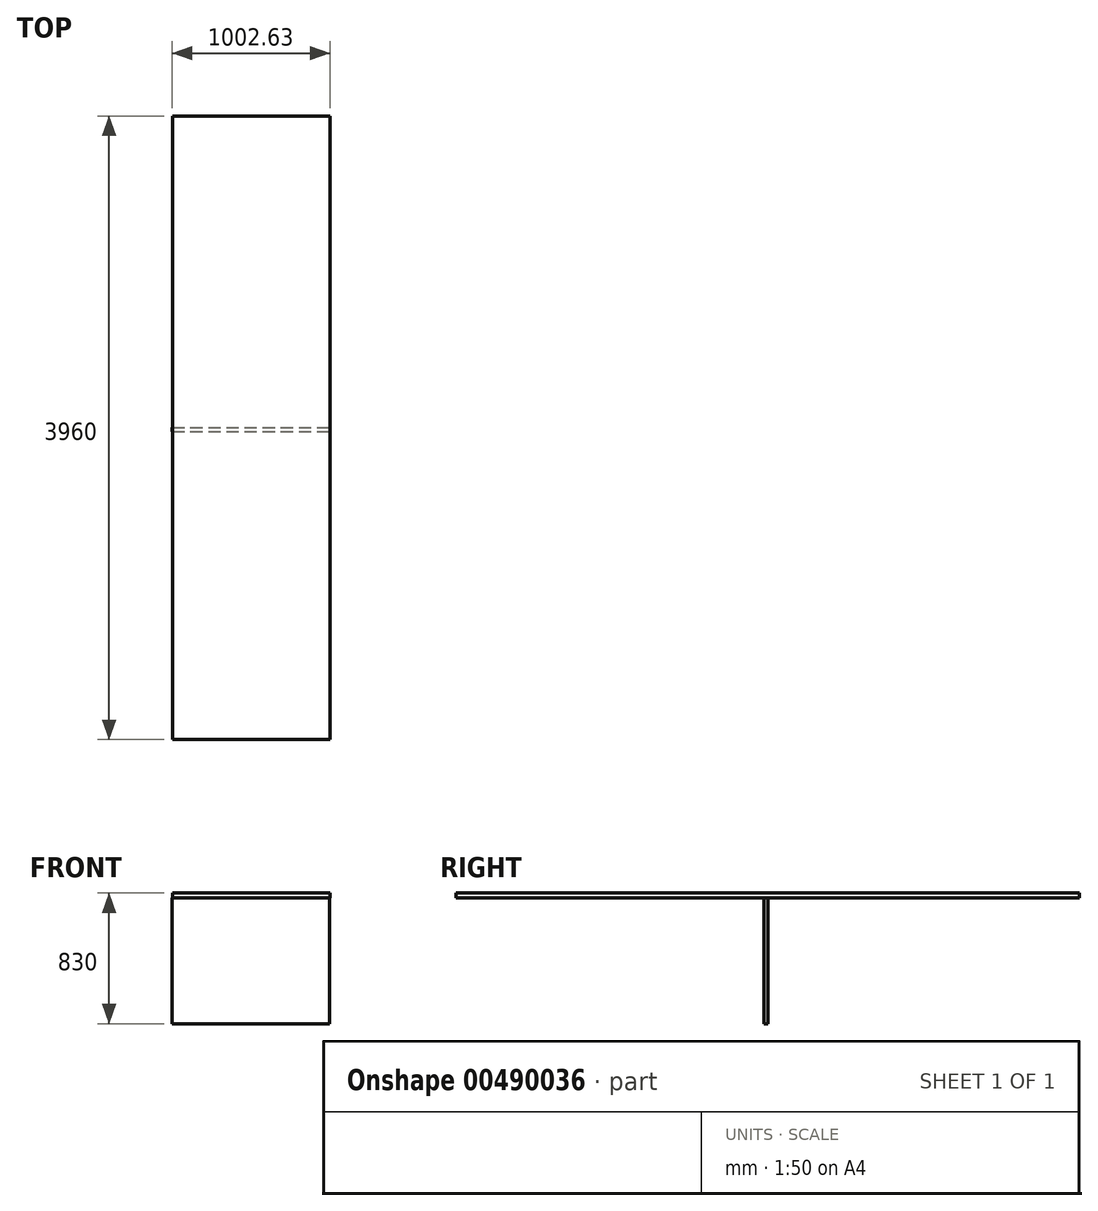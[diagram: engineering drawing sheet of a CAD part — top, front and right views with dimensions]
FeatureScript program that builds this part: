
annotation { "Feature Type Name" : "Feature", "Feature Type Description" : "" }
export const myFeature = defineFeature(function(context is Context, id is Id, definition is map)
    precondition{}
    {
        {
            var Q0;
            Q0=qCreatedBy(makeId("Top.planeOp"),FACE);
            var sketch = newSketch(context, id + "F0", { "sketchPlane" : qUnion([Q0])});
            skLineSegment(sketch, "E0.bottom", {"start": v(500, 500) * mm, "end": v(-500, 500) * mm});
            skLineSegment(sketch, "E0.top", {"start": v(500, -500) * mm, "end": v(-500, -500) * mm});
            skLineSegment(sketch, "E0.left", {"start": v(500, 500) * mm, "end": v(500, -500) * mm});
            skLineSegment(sketch, "E0.right", {"start": v(-500, 500) * mm, "end": v(-500, -500) * mm});
            skPoint(sketch, "E0.middle", {"position": v(0, 0) * mm});
            skLineSegment(sketch, "E1.top", {"start": v(500, 1250) * mm, "end": v(-500, 1250) * mm});
            skLineSegment(sketch, "E1.left", {"start": v(500, 500) * mm, "end": v(500, 1250) * mm});
            skLineSegment(sketch, "E1.right", {"start": v(-500, 500) * mm, "end": v(-500, 1250) * mm});
            skLineSegment(sketch, "E2.top", {"start": v(500, -1250) * mm, "end": v(-500, -1250) * mm});
            skLineSegment(sketch, "E2.left", {"start": v(500, -500) * mm, "end": v(500, -1250) * mm});
            skLineSegment(sketch, "E2.right", {"start": v(-500, -500) * mm, "end": v(-500, -1250) * mm});
            skLineSegment(sketch, "E3.top", {"start": v(500, 1980) * mm, "end": v(-500, 1980) * mm});
            skLineSegment(sketch, "E3.left", {"start": v(500, 1250) * mm, "end": v(500, 1980) * mm});
            skLineSegment(sketch, "E3.right", {"start": v(-500, 1250) * mm, "end": v(-500, 1980) * mm});
            skLineSegment(sketch, "E4.top", {"start": v(500, -1980) * mm, "end": v(-500, -1980) * mm});
            skLineSegment(sketch, "E4.left", {"start": v(500, -1250) * mm, "end": v(500, -1980) * mm});
            skLineSegment(sketch, "E4.right", {"start": v(-500, -1250) * mm, "end": v(-500, -1980) * mm});
            skLineSegment(sketch, "E5", {"start": v(500, 0) * mm, "end": v(-500, -875) * mm});
            skLineSegment(sketch, "E6", {"start": v(-500, -875) * mm, "end": v(500, -1980) * mm});
            skLineSegment(sketch, "E7", {"start": v(500, 0) * mm, "end": v(-500, 953.53) * mm});
            skLineSegment(sketch, "E8", {"start": v(-500, 953.53) * mm, "end": v(500, 1980) * mm});
            skSolve(sketch);
        }
        {
            var Q0;
            Q0=qCreatedBy(makeId("Front.planeOp"),FACE);
            var sketch = newSketch(context, id + "F1", { "sketchPlane" : qUnion([Q0])});
            skLineSegment(sketch, "E9.bottom", {"start": v(-502.63, 0) * mm, "end": v(497.37, 0) * mm});
            skLineSegment(sketch, "E9.top", {"start": v(-502.63, -800) * mm, "end": v(497.37, -800) * mm});
            skLineSegment(sketch, "E9.left", {"start": v(-502.63, 0) * mm, "end": v(-502.63, -800) * mm});
            skLineSegment(sketch, "E9.right", {"start": v(497.37, 0) * mm, "end": v(497.37, -800) * mm});
            skPoint(sketch, "E10", {"position": v(-3200.93, -10902.9) * mm});
            skPoint(sketch, "E11.0", {"position": v(-500, 0) * mm});
            skSolve(sketch);
        }
        {
            var Q0;
            Q0=sQuery(id+"F0.wireOp",EDGE,"E7");
            var Q1;
            Q1=sQuery(id+"F0.wireOp",EDGE,"E8");
            var Q2;
            Q2=sQuery(id+"F0.wireOp",EDGE,"E5");
            var Q3;
            Q3=sQuery(id+"F0.wireOp",EDGE,"E6");
            extrude(context, id + "F2", {"bodyType" : ToolBodyType.SURFACE, "surfaceEntities" : qUnion([Q0, Q1, Q2, Q3]), "oppositeDirection" : true, "depth" : 800 * mm});
        }
        {
            var Q0;
            Q0 = qSketchRegion(id + "F0", true);
            extrude(context, id + "F3", {"entities" : qUnion([Q0]), "depth" : 30 * mm});
        }
        {
            var Q0;
            Q0=makeQuery(id+"F1.imprint","IMPRINT",FACE,{"disambiguationData":[TD([[makeQuery(id+"F1.imprint","IMPRINT",EDGE,{"derivedFrom":sQuery(id+"F1.wireOp",EDGE,"E9.bottom")}),-1.0]])]});
            extrude(context, id + "F4", {"entities" : qUnion([Q0]), "operationType" : NewBodyOperationType.ADD, "depth" : 25 * mm});
        }
    });
